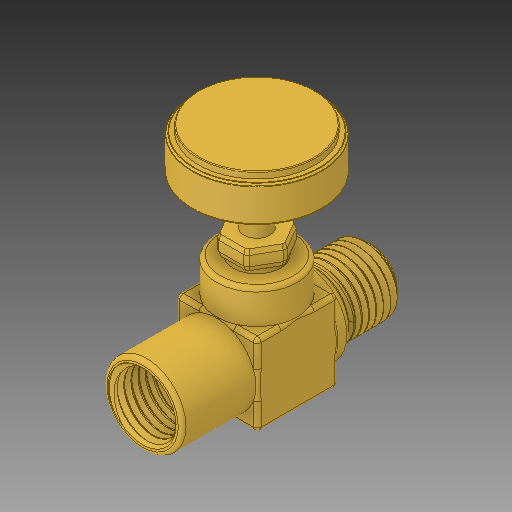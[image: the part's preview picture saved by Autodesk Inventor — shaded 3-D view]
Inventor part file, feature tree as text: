
AUTODESK INVENTOR PART (.ipt)
format: ipt  version: 2018 (Build 220112000, 112)  size: 1,808,384 bytes
history: native  units: in
note: dims shown in document units (in); Inventor stores cm internally (conversion verified against a paired STEP export)
features: fillet x1
ambient origin geometry x8: Origin, YZ Plane, XZ Plane, XY Plane, X Axis, Y Axis, Z Axis, Center Point
bodies: Solid1 (feature_tree)
feature tree (1):
  fillet  "Fillet2"  [1 undecoded]
note: 1 required parameter value undecoded (feature->parameter linkage not recoverable at this tier; creation-order binding heuristic only, values carry confidence <= 0.55)
